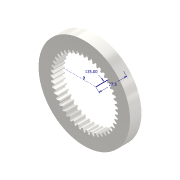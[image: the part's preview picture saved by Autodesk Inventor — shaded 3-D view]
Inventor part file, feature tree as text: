
AUTODESK INVENTOR PART (.ipt)
format: ipt  version: 2020.2 (Build 242310000, 310)  size: 455,168 bytes
history: native  units: mm (DEFAULTED — no unit token found)
features: other x4, sketch x4, extrude x3, plane x3, direct_edit x1
ambient origin geometry x8: Origin, YZ Plane, XZ Plane, XY Plane, X Axis, Y Axis, Z Axis, Center Point
bodies: Solid1 (feature_tree)
feature tree (15):
  extrude  "Extrusion1"  Depth=8.0mm TaperAngle=0.0deg
  plane  "Work Plane2"
  plane  "Work Plane8"
  plane  "Work Plane9"
  other  "Spur Gear"
  direct_edit  "Direct Edit1"
  extrude  "Extrusion2"  Depth=10.0mm TaperAngle=0.0deg
  extrude  "Extrusion3"  Depth=0.698132mm TaperAngle=0.0deg
  sketch  "Sketch1"  dims[d0=52.25mm d1=8.0mm d2=0.0mm]
  sketch  "Sketch2"  dims[d3=45.0mm d4=10.0mm d5=0.0mm]
  other  "Srf1"
  sketch  "Sketch3"  dims[d16=15.0mm d17=0.0mm d34=0.698132mm]
  sketch  "Sketch4"  dims[d39=0.0mm d45=0.0mm d47=15.0mm d50=0.0mm d51=0.0mm d52=15.0mm d53=6.0mm d54=27.5mm d55=135.0deg d56=27.5mm d57=45.0deg d58=3.0mm d59=3.0mm d60=0.0mm d61=0.0mm d62=6.0mm d63=6.0mm d64=2.0mm d65=0.0mm]
  other  "Pitch Diameter"
  other  "Size1"
